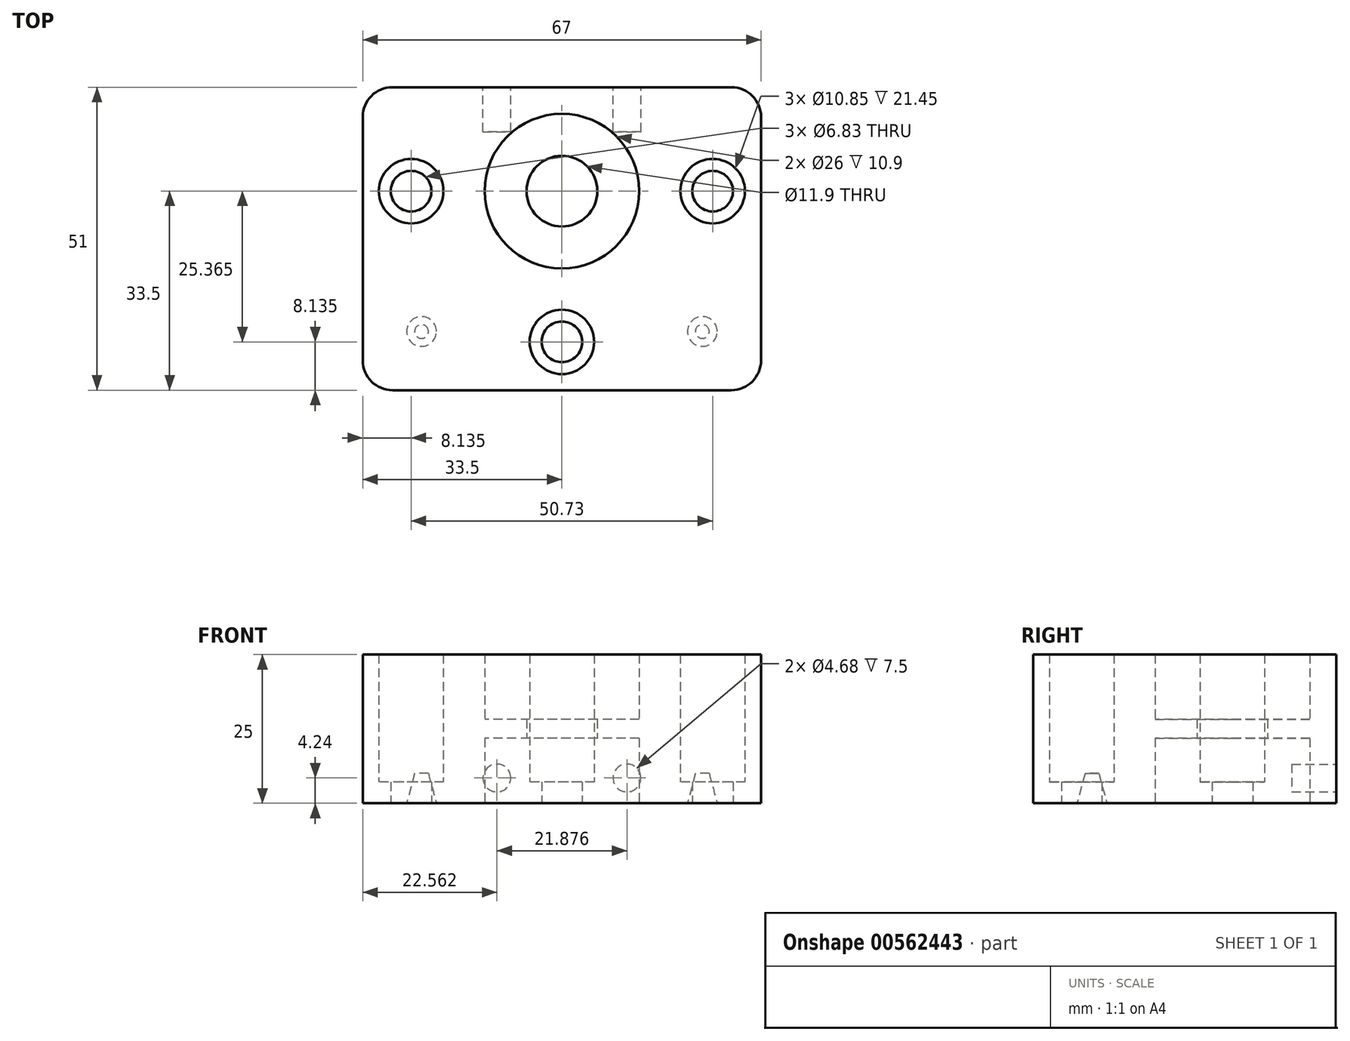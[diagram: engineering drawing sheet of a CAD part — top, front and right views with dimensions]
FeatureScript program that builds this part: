
annotation { "Feature Type Name" : "Feature", "Feature Type Description" : "" }
export const myFeature = defineFeature(function(context is Context, id is Id, definition is map)
    precondition{}
    {
        {
            var Q0;
            Q0=qCreatedBy(makeId("Top.planeOp"),FACE);
            var sketch = newSketch(context, id + "F0", { "sketchPlane" : qUnion([Q0])});
            skLineSegment(sketch, "E0.bottom", {"start": v(-33.5, 17.5) * mm, "end": v(33.5, 17.5) * mm});
            skLineSegment(sketch, "E0.top", {"start": v(-33.5, -33.5) * mm, "end": v(33.5, -33.5) * mm});
            skLineSegment(sketch, "E0.left", {"start": v(-33.5, 17.5) * mm, "end": v(-33.5, -33.5) * mm});
            skLineSegment(sketch, "E0.right", {"start": v(33.5, 17.5) * mm, "end": v(33.5, -33.5) * mm});
            skCircle(sketch, "E1", {"center": v(0, 0) * mm, "radius": 5.95 * mm});
            skCircle(sketch, "E2", {"center": v(25.37, 0) * mm, "radius": 3.42 * mm});
            skCircle(sketch, "E3", {"center": v(-25.37, 0) * mm, "radius": 3.42 * mm});
            skLineSegment(sketch, "E4.bottom", {"start": v(-14.98, 17.5) * mm, "end": v(14.98, 17.5) * mm});
            skLineSegment(sketch, "E4.top", {"start": v(-14.98, -33.5) * mm, "end": v(14.98, -33.5) * mm});
            skLineSegment(sketch, "E4.left", {"start": v(-14.98, 17.5) * mm, "end": v(-14.98, -33.5) * mm});
            skLineSegment(sketch, "E4.right", {"start": v(14.98, 17.5) * mm, "end": v(14.98, -33.5) * mm});
            skCircle(sketch, "E5", {"center": v(-25.37, 0) * mm, "radius": 5.42 * mm});
            skCircle(sketch, "E6", {"center": v(25.37, 0) * mm, "radius": 5.42 * mm});
            skCircle(sketch, "E7", {"center": v(0, -25.37) * mm, "radius": 3.42 * mm});
            skCircle(sketch, "E8", {"center": v(0, -25.37) * mm, "radius": 5.42 * mm});
            skSolve(sketch);
        }
        {
            var Q0;
            Q0=makeQuery(id+"F0.imprint","IMPRINT",FACE,{"disambiguationData":[TD([[makeQuery(id+"F0.imprint","IMPRINT",EDGE,{"derivedFrom":sQuery(id+"F0.wireOp",EDGE,"E1")}),-1.0]])]});
            extrude(context, id + "F1", {"entities" : qUnion([Q0]), "depth" : 25 * mm});
        }
        {
            var Q0;
            {var subQ1=sQuery(id+"F0.wireOp",EDGE,"E0.left");Q0=makeQuery(id+"F0.imprint","IMPRINT",FACE,{"disambiguationData":[TD([[makeQuery(id+"F0.imprint","IMPRINT",EDGE,{"derivedFrom":subQ1}),1.0]])]});}
            var Q1;
            {var subQ1=sQuery(id+"F0.wireOp",EDGE,"E0.right");Q1=makeQuery(id+"F0.imprint","IMPRINT",FACE,{"disambiguationData":[TD([[makeQuery(id+"F0.imprint","IMPRINT",EDGE,{"derivedFrom":subQ1}),-1.0]])]});}
            extrude(context, id + "F2", {"entities" : qUnion([Q0, Q1]), "operationType" : NewBodyOperationType.ADD, "depth" : 25 * mm});
        }
        {
            var Q0;
            Q0=makeQuery(id+"F0.imprint","IMPRINT",FACE,{"disambiguationData":[TD([[makeQuery(id+"F0.imprint","IMPRINT",EDGE,{"derivedFrom":sQuery(id+"F0.wireOp",EDGE,"E3")}),-1.0]])]});
            var Q1;
            Q1=makeQuery(id+"F0.imprint","IMPRINT",FACE,{"disambiguationData":[TD([[makeQuery(id+"F0.imprint","IMPRINT",EDGE,{"derivedFrom":sQuery(id+"F0.wireOp",EDGE,"E2")}),-1.0]])]});
            var Q2;
            Q2=makeQuery(id+"F0.imprint","IMPRINT",FACE,{"disambiguationData":[TD([[makeQuery(id+"F0.imprint","IMPRINT",EDGE,{"derivedFrom":sQuery(id+"F0.wireOp",EDGE,"E7")}),-1.0]])]});
            extrude(context, id + "F3", {"entities" : qUnion([Q0, Q1, Q2]), "operationType" : NewBodyOperationType.ADD, "depth" : 3.55 * mm});
        }
        {
            var Q0;
            {var subQ0=sQuery(id+"F0.wireOp",EDGE,"E0.bottom");var subQ1=sQuery(id+"F0.wireOp",EDGE,"E4.bottom");var subQ2=makeQuery(id+"F0.imprint","IMPRINT",EDGE,{"disambiguationData":[TD([[makeQuery(id+"F0.imprint","INTERSECT",VERTEX,{"derivedFrom":[subQ0,sQuery(id+"F0.wireOp",EDGE,"E0.right")]}),1.0]])],"derivedFrom":subQ0});var subQ3=makeQuery(id+"F0.imprint","IMPRINT",EDGE,{"disambiguationData":[TD([[makeQuery(id+"F0.imprint","INTERSECT",VERTEX,{"derivedFrom":[subQ0,sQuery(id+"F0.wireOp",EDGE,"E0.left")]}),-1.0]])],"derivedFrom":subQ0});Q0=makeQuery(id+"FTeboLwCj6z0h2F_3.boolean.opBoolean","MERGE",FACE,{"derivedFrom":[makeQuery(id+"FI1iS4n02Gt5v50_0.boolean.opBoolean","MERGE",FACE,{"derivedFrom":[makeQuery(id+"F2.boolean.opBoolean","MERGE",FACE,{"derivedFrom":[makeQuery(id+"F1.opExtrude","SWEPT_FACE",FACE,{"disambiguationData":[OSD([subQ1])]}),makeQuery(id+"F2.opExtrude","SWEPT_FACE",FACE,{"disambiguationData":[OSD([subQ0]),TDD([subQ3])]}),makeQuery(id+"F2.opExtrude","SWEPT_FACE",FACE,{"disambiguationData":[OSD([subQ0]),TDD([subQ2])]})]}),makeQuery(id+"FI1iS4n02Gt5v50_0.opExtrude","SWEPT_FACE",FACE,{"disambiguationData":[OSD([subQ0,subQ1])]})]}),makeQuery(id+"FTeboLwCj6z0h2F_3.opExtrude","SWEPT_FACE",FACE,{"disambiguationData":[OSD([subQ0]),TDD([subQ3])]}),makeQuery(id+"FTeboLwCj6z0h2F_3.opExtrude","SWEPT_FACE",FACE,{"disambiguationData":[OSD([subQ0]),TDD([subQ2])]})]});}
            var sketch = newSketch(context, id + "F4", { "sketchPlane" : qUnion([Q0])});
            skCircle(sketch, "E9", {"center": v(-10.94, 4.24) * mm, "radius": 2.34 * mm});
            skCircle(sketch, "E10", {"center": v(10.94, 4.24) * mm, "radius": 2.34 * mm});
            skSolve(sketch);
        }
        {
            var Q0;
            Q0=makeQuery(id+"F4.imprint","IMPRINT",FACE,{"disambiguationData":[TD([[makeQuery(id+"F4.imprint","IMPRINT",EDGE,{"derivedFrom":sQuery(id+"F4.wireOp",EDGE,"E9")}),1.0]])]});
            var Q1;
            Q1=makeQuery(id+"F4.imprint","IMPRINT",FACE,{"disambiguationData":[TD([[makeQuery(id+"F4.imprint","IMPRINT",EDGE,{"derivedFrom":sQuery(id+"F4.wireOp",EDGE,"E10")}),1.0]])]});
            var Q2;
            Q2=sQuery(id+"F4.wireOp",EDGE,"E9");
            var Q3;
            Q3=sQuery(id+"F4.wireOp",EDGE,"E10");
            extrude(context, id + "F5", {"entities" : qUnion([Q0, Q1]), "operationType" : NewBodyOperationType.REMOVE, "surfaceEntities" : qUnion([Q2, Q3]), "oppositeDirection" : true, "depth" : 7.5 * mm});
        }
        {
            var Q0;
            Q0=qCreatedBy(makeId("Top.planeOp"),FACE);
            var sketch = newSketch(context, id + "F6", { "sketchPlane" : qUnion([Q0])});
            skCircle(sketch, "E11", {"center": v(0, 0) * mm, "radius": 13 * mm});
            skSolve(sketch);
        }
        {
            var Q0;
            Q0=qSketchRegion(id+"F6",true);
            extrude(context, id + "F7", {"entities" : qUnion([Q0]), "operationType" : NewBodyOperationType.REMOVE, "depth" : 25 * mm, "hasSecondDirection" : true, "secondDirectionOppositeDirection" : false, "secondDirectionDepth" : 14.1 * mm});
        }
        {
            var Q0;
            Q0=qSketchRegion(id+"F6",true);
            extrude(context, id + "F8", {"entities" : qUnion([Q0]), "operationType" : NewBodyOperationType.REMOVE, "depth" : 10.9 * mm});
        }
        {
            var Q0;
            Q0=qCreatedBy(makeId("Top.planeOp"),FACE);
            var sketch = newSketch(context, id + "F9", { "sketchPlane" : qUnion([Q0])});
            skLineSegment(sketch, "E12.rect.bottom", {"start": v(-28.11, 28.11) * mm, "end": v(28.12, 28.11) * mm});
            skLineSegment(sketch, "E12.rect.top", {"start": v(-28.12, -28.11) * mm, "end": v(28.11, -28.11) * mm});
            skLineSegment(sketch, "E12.rect.left", {"start": v(-28.11, 28.12) * mm, "end": v(-28.12, -28.11) * mm});
            skLineSegment(sketch, "E12.rect.right", {"start": v(28.12, 28.12) * mm, "end": v(28.11, -28.11) * mm});
            skPoint(sketch, "E12.rect.middle", {"position": v(0, 0) * mm});
            skCircle(sketch, "E13", {"center": v(0, 0) * mm, "radius": 19.04 * mm});
            skCircle(sketch, "E14", {"center": v(0, 0) * mm, "radius": 3.98 * mm});
            skCircle(sketch, "E15", {"center": v(-23.62, 23.62) * mm, "radius": 2.5 * mm});
            skCircle(sketch, "E16", {"center": v(23.62, 23.62) * mm, "radius": 2.5 * mm});
            skCircle(sketch, "E17", {"center": v(23.62, -23.62) * mm, "radius": 2.5 * mm});
            skCircle(sketch, "E18", {"center": v(-23.62, -23.62) * mm, "radius": 2.5 * mm});
            skLineSegment(sketch, "E19.rect.bottom", {"start": v(-23.62, 23.62) * mm, "end": v(23.62, 23.62) * mm, "construction": true});
            skLineSegment(sketch, "E19.rect.top", {"start": v(-23.62, -23.62) * mm, "end": v(23.62, -23.62) * mm, "construction": true});
            skLineSegment(sketch, "E19.rect.left", {"start": v(-23.62, 23.62) * mm, "end": v(-23.62, -23.62) * mm, "construction": true});
            skLineSegment(sketch, "E19.rect.right", {"start": v(23.62, 23.62) * mm, "end": v(23.62, -23.62) * mm, "construction": true});
            skCircle(sketch, "E20", {"center": v(0, 0) * mm, "radius": 5.38 * mm});
            skSolve(sketch);
        }
        {
            var Q0;
            Q0=makeQuery(id+"F9.imprint","IMPRINT",FACE,{"disambiguationData":[TD([[makeQuery(id+"F9.imprint","IMPRINT",EDGE,{"derivedFrom":sQuery(id+"F9.wireOp",EDGE,"E17")}),1.0]])]});
            var Q1;
            Q1=makeQuery(id+"F9.imprint","IMPRINT",FACE,{"disambiguationData":[TD([[makeQuery(id+"F9.imprint","IMPRINT",EDGE,{"derivedFrom":sQuery(id+"F9.wireOp",EDGE,"E18")}),1.0]])]});
            var Q2;
            Q2=sQuery(id+"F9.wireOp",EDGE,"E17");
            var Q3;
            Q3=sQuery(id+"F9.wireOp",EDGE,"E18");
            extrude(context, id + "F10", {"entities" : qUnion([Q0, Q1]), "operationType" : NewBodyOperationType.REMOVE, "surfaceEntities" : qUnion([Q2, Q3]), "depth" : 5 * mm, "hasDraft" : true, "draftAngle" : 15 * degree, "draftPullDirection" : true});
        }
        {
            var Q0;
            Q0=makeQuery(id+"F2.opExtrude","SWEPT_EDGE",EDGE,{"disambiguationData":[OSD([sQuery(id+"F0.wireOp",EDGE,"E0.top"),sQuery(id+"F0.wireOp",EDGE,"E0.right")])]});
            var Q1;
            Q1=makeQuery(id+"F2.opExtrude","SWEPT_EDGE",EDGE,{"disambiguationData":[OSD([sQuery(id+"F0.wireOp",EDGE,"E0.top"),sQuery(id+"F0.wireOp",EDGE,"E0.left")])]});
            var Q2;
            Q2=makeQuery(id+"F2.opExtrude","SWEPT_EDGE",EDGE,{"disambiguationData":[OSD([sQuery(id+"F0.wireOp",EDGE,"E0.bottom"),sQuery(id+"F0.wireOp",EDGE,"E0.left")])]});
            var Q3;
            Q3=makeQuery(id+"F2.opExtrude","SWEPT_EDGE",EDGE,{"disambiguationData":[OSD([sQuery(id+"F0.wireOp",EDGE,"E0.bottom"),sQuery(id+"F0.wireOp",EDGE,"E0.right")])]});
            fillet(context, id + "F11", {"entities" : qUnion([Q0, Q1, Q2, Q3]), "radius" : 5 * mm, "tangentPropagation" : true, "allowEdgeOverflow" : false});
        }
    });
